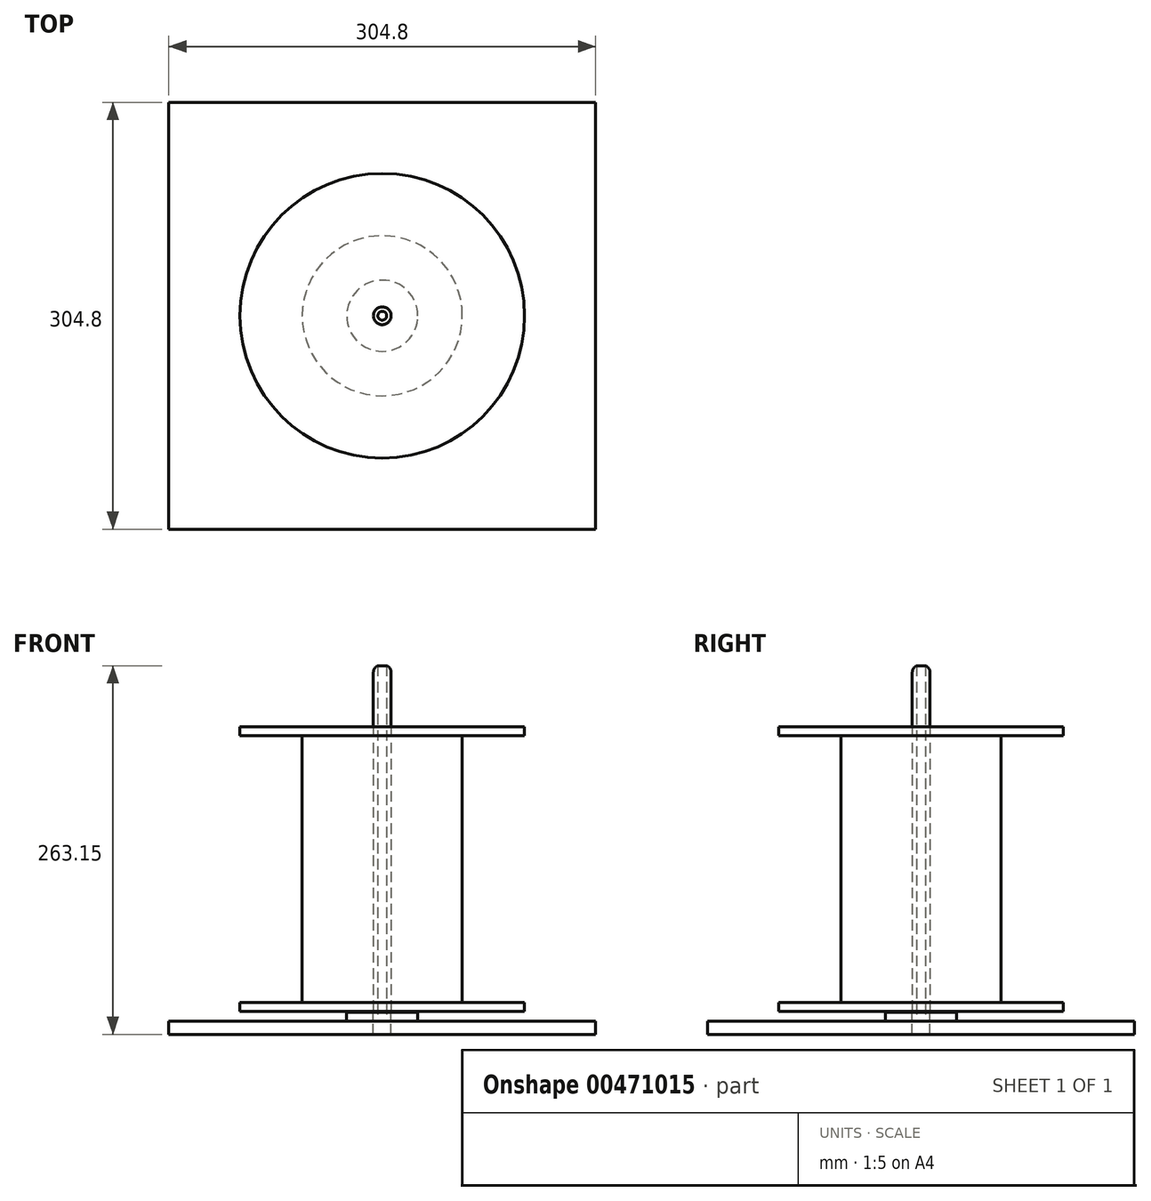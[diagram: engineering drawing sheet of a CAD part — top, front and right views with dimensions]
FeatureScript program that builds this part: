
annotation { "Feature Type Name" : "Feature", "Feature Type Description" : "" }
export const myFeature = defineFeature(function(context is Context, id is Id, definition is map)
    precondition{}
    {
        {
            var Q0;
            Q0=qCreatedBy(makeId("Top.planeOp"),FACE);
            var sketch = newSketch(context, id + "F0", { "sketchPlane" : qUnion([Q0])});
            skLineSegment(sketch, "E0.bottom", {"start": v(-152.4, 152.4) * mm, "end": v(152.4, 152.4) * mm});
            skLineSegment(sketch, "E0.top", {"start": v(-152.4, -152.4) * mm, "end": v(152.4, -152.4) * mm});
            skLineSegment(sketch, "E0.left", {"start": v(-152.4, 152.4) * mm, "end": v(-152.4, -152.4) * mm});
            skLineSegment(sketch, "E0.right", {"start": v(152.4, 152.4) * mm, "end": v(152.4, -152.4) * mm});
            skSolve(sketch);
        }
        {
            var Q0;
            Q0 = qSketchRegion(id + "F0", true);
            extrude(context, id + "F1", {"entities" : qUnion([Q0]), "depth" : 9.52 * mm, "offsetDistance" : 25.4 * mm});
        }
        {
            var Q0;
            Q0=makeQuery(id+"F1.opExtrude","CAP_FACE",FACE,{"disambiguationData":[OSD([sQuery(id+"F0.wireOp",EDGE,"E0.bottom"),sQuery(id+"F0.wireOp",EDGE,"E0.top"),sQuery(id+"F0.wireOp",EDGE,"E0.left"),sQuery(id+"F0.wireOp",EDGE,"E0.right")])],"isStart":false});
            var sketch = newSketch(context, id + "F2", { "sketchPlane" : qUnion([Q0])});
            skCircle(sketch, "E1", {"center": v(0, 0) * mm, "radius": 25.4 * mm});
            skSolve(sketch);
        }
        {
            var Q0;
            Q0 = qSketchRegion(id + "F2", true);
            extrude(context, id + "F3", {"entities" : qUnion([Q0]), "depth" : 6.35 * mm, "offsetDistance" : 25.4 * mm});
        }
        {
            var Q0;
            Q0=makeQuery(id+"F3.opExtrude","CAP_FACE",FACE,{"disambiguationData":[OSD([sQuery(id+"F2.wireOp",EDGE,"E1")])],"isStart":false});
            var sketch = newSketch(context, id + "F4", { "sketchPlane" : qUnion([Q0])});
            skCircle(sketch, "E2", {"center": v(0, 0) * mm, "radius": 6.35 * mm});
            skSolve(sketch);
        }
        {
            var Q0;
            Q0 = qSketchRegion(id + "F4", true);
            extrude(context, id + "F5", {"entities" : qUnion([Q0]), "operationType" : NewBodyOperationType.REMOVE, "endBound" : BoundingType.THROUGH_ALL, "oppositeDirection" : true, "depth" : 25.4 * mm, "offsetDistance" : 25.4 * mm});
        }
        {
            var Q0;
            Q0=makeQuery(id+"F1.opExtrude","CAP_FACE",FACE,{"disambiguationData":[OSD([sQuery(id+"F0.wireOp",EDGE,"E0.bottom"),sQuery(id+"F0.wireOp",EDGE,"E0.top"),sQuery(id+"F0.wireOp",EDGE,"E0.left"),sQuery(id+"F0.wireOp",EDGE,"E0.right")])],"isStart":false});
            var sketch = newSketch(context, id + "F6", { "sketchPlane" : qUnion([Q0])});
            skCircle(sketch, "E3", {"center": v(0, 0) * mm, "radius": 6.35 * mm});
            skSolve(sketch);
        }
        {
            var Q0;
            Q0 = qSketchRegion(id + "F6", true);
            extrude(context, id + "F7", {"entities" : qUnion([Q0]), "depth" : 254 * mm, "offsetDistance" : 25.4 * mm});
        }
        {
            var Q0;
            Q0=makeQuery(id+"F7.opExtrude","CAP_EDGE",EDGE,{"disambiguationData":[OSD([sQuery(id+"F6.wireOp",EDGE,"E3")])],"isStart":false});
            fillet(context, id + "F8", {"entities" : qUnion([Q0]), "radius" : 5.08 * mm, "tangentPropagation" : true, "allowEdgeOverflow" : false});
        }
        {
            var Q0;
            Q0=makeQuery(id+"F1.opExtrude","CAP_FACE",FACE,{"disambiguationData":[OSD([sQuery(id+"F0.wireOp",EDGE,"E0.bottom"),sQuery(id+"F0.wireOp",EDGE,"E0.top"),sQuery(id+"F0.wireOp",EDGE,"E0.left"),sQuery(id+"F0.wireOp",EDGE,"E0.right")])],"isStart":true});
            var sketch = newSketch(context, id + "F9", { "sketchPlane" : qUnion([Q0])});
            skCircle(sketch, "E4", {"center": v(0, 0) * mm, "radius": 3.18 * mm});
            skSolve(sketch);
        }
        {
            var Q0;
            Q0 = qSketchRegion(id + "F9", true);
            extrude(context, id + "F10", {"entities" : qUnion([Q0]), "operationType" : NewBodyOperationType.REMOVE, "endBound" : BoundingType.THROUGH_ALL, "oppositeDirection" : true, "depth" : 25.4 * mm, "offsetDistance" : 25.4 * mm});
        }
        {
            var Q0;
            Q0=makeQuery(id+"F1.opExtrude","CAP_FACE",FACE,{"disambiguationData":[OSD([sQuery(id+"F0.wireOp",EDGE,"E0.bottom"),sQuery(id+"F0.wireOp",EDGE,"E0.top"),sQuery(id+"F0.wireOp",EDGE,"E0.left"),sQuery(id+"F0.wireOp",EDGE,"E0.right")])],"isStart":true});
            var sketch = newSketch(context, id + "F11", { "sketchPlane" : qUnion([Q0])});
            skCircle(sketch, "E5", {"center": v(0, 0) * mm, "radius": 4.76 * mm});
            skSolve(sketch);
        }
        {
            var Q0;
            Q0 = qSketchRegion(id + "F11", true);
            extrude(context, id + "F12", {"entities" : qUnion([Q0]), "operationType" : NewBodyOperationType.REMOVE, "oppositeDirection" : true, "depth" : 6.6 * mm, "offsetDistance" : 25.4 * mm});
        }
        {
            var Q0;
            Q0=makeQuery(id+"F7.opExtrude","CAP_FACE",FACE,{"disambiguationData":[OSD([sQuery(id+"F6.wireOp",EDGE,"E3")])],"isStart":true});
            var sketch = newSketch(context, id + "F13", { "sketchPlane" : qUnion([Q0])});
            skCircle(sketch, "E6", {"center": v(0, 0) * mm, "radius": 2.54 * mm});
            skSolve(sketch);
        }
        {
            var Q0;
            Q0 = qSketchRegion(id + "F13", true);
            extrude(context, id + "F14", {"entities" : qUnion([Q0]), "operationType" : NewBodyOperationType.REMOVE, "oppositeDirection" : true, "depth" : 19.05 * mm, "offsetDistance" : 25.4 * mm});
        }
        {
            var Q0;
            Q0=qCreatedBy(makeId("Front.planeOp"),FACE);
            var sketch = newSketch(context, id + "F15", { "sketchPlane" : qUnion([Q0])});
            skLineSegment(sketch, "E7", {"start": v(0, 0) * mm, "end": v(0, 256.43) * mm, "construction": true});
            skLineSegment(sketch, "E8", {"start": v(-6.35, 16.51) * mm, "end": v(-101.6, 16.5) * mm});
            skLineSegment(sketch, "E9", {"start": v(-101.6, 16.5) * mm, "end": v(-101.6, 22.86) * mm});
            skLineSegment(sketch, "E10", {"start": v(-101.6, 22.86) * mm, "end": v(-57.15, 22.86) * mm});
            skLineSegment(sketch, "E11", {"start": v(-57.15, 22.86) * mm, "end": v(-57.15, 213.36) * mm});
            skLineSegment(sketch, "E12", {"start": v(-57.15, 213.36) * mm, "end": v(-101.6, 213.36) * mm});
            skLineSegment(sketch, "E13", {"start": v(-101.6, 213.36) * mm, "end": v(-101.6, 219.71) * mm});
            skLineSegment(sketch, "E14", {"start": v(-101.6, 219.71) * mm, "end": v(-6.35, 219.71) * mm});
            skLineSegment(sketch, "E15", {"start": v(0, 219.71) * mm, "end": v(0, 16.5) * mm});
            skLineSegment(sketch, "E16", {"start": v(-6.35, 219.71) * mm, "end": v(-6.35, 16.5) * mm});
            skSolve(sketch);
        }
        {
            var Q0;
            Q0=makeQuery(id+"F15.imprint","IMPRINT",FACE,{"disambiguationData":[TD([[makeQuery(id+"F15.imprint","IMPRINT",EDGE,{"derivedFrom":sQuery(id+"F15.wireOp",EDGE,"E8")}),-1.0]])]});
            var Q1;
            Q1=sQuery(id+"F15.wireOp",EDGE,"E7");
            revolve(context, id + "F16", {"entities" : qUnion([Q0]), "axis" : qUnion([Q1]), "revolveType" : RevolveType.FULL});
        }
    });
